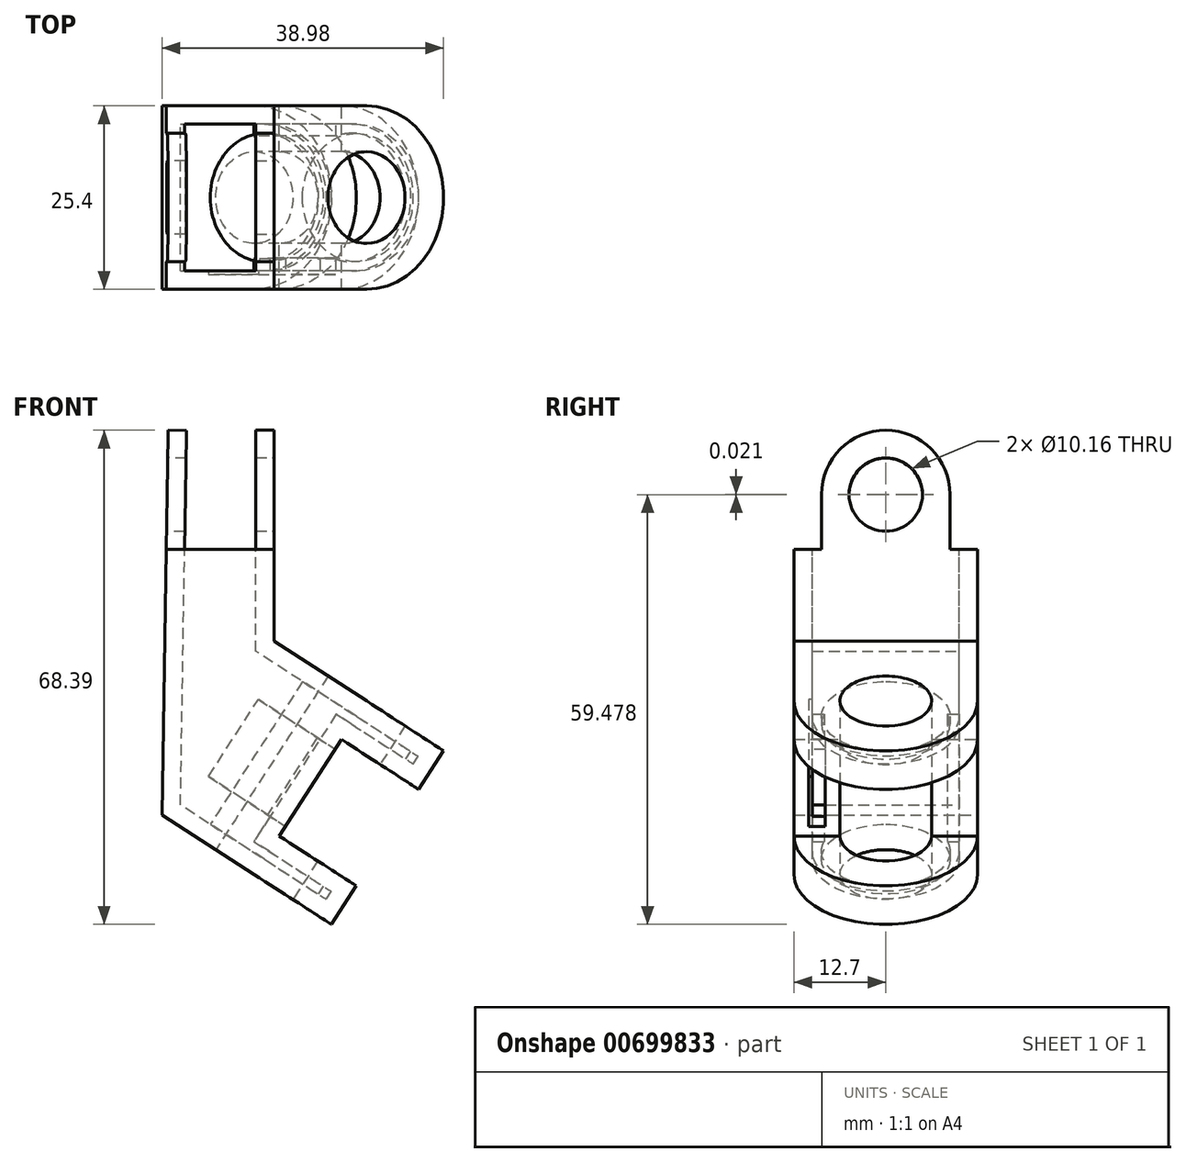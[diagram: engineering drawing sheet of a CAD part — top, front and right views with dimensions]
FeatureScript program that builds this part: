
annotation { "Feature Type Name" : "Feature", "Feature Type Description" : "" }
export const myFeature = defineFeature(function(context is Context, id is Id, definition is map)
    precondition{}
    {
        {
            var Q0;
            Q0=qCreatedBy(makeId("Front.planeOp"),FACE);
            var sketch = newSketch(context, id + "F0", { "sketchPlane" : qUnion([Q0])});
            skLineSegment(sketch, "E0", {"start": v(3.05, 0.95) * mm, "end": v(-9.73, 9.2) * mm});
            skLineSegment(sketch, "E1", {"start": v(-12.48, -23.08) * mm, "end": v(-25.26, -14.82) * mm});
            skLineSegment(sketch, "E2", {"start": v(-9.73, 9.2) * mm, "end": v(-9.73, 21.9) * mm});
            skLineSegment(sketch, "E3", {"start": v(-24.67, 21.9) * mm, "end": v(-9.73, 21.9) * mm});
            skLineSegment(sketch, "E4", {"start": v(-10.92, -20.66) * mm, "end": v(1.49, -1.46) * mm});
            skPoint(sketch, "E5.start.orphan", {"position": v(4.25, -16.85) * mm});
            skLineSegment(sketch, "E6", {"start": v(-10.92, -20.66) * mm, "end": v(-12.48, -23.08) * mm});
            skLineSegment(sketch, "E7", {"start": v(-12.48, -23.08) * mm, "end": v(3.05, 0.95) * mm});
            skPoint(sketch, "E8.orphan", {"position": v(-3.52, -28.87) * mm});
            skPoint(sketch, "E9.start.orphan", {"position": v(-1.96, -26.45) * mm});
            skPoint(sketch, "E10.start.orphan", {"position": v(10.45, -7.25) * mm});
            skPoint(sketch, "E11.orphan", {"position": v(12, -4.84) * mm});
            skLineSegment(sketch, "E12", {"start": v(-25.26, -14.82) * mm, "end": v(-24.67, 21.9) * mm});
            skSolve(sketch);
        }
        {
            var Q0;
            Q0=qSketchRegion(id+"F0",true);
            extrude(context, id + "F1", {"entities" : qUnion([Q0]), "depth" : 25.4 * mm});
        }
        {
            var Q0;
            Q0=makeQuery(id+"F1.opExtrude","SWEPT_FACE",FACE,{"disambiguationData":[OSD([sQuery(id+"F0.wireOp",EDGE,"E0")])]});
            var sketch = newSketch(context, id + "F2", { "sketchPlane" : qUnion([Q0])});
            skLineSegment(sketch, "E13", {"start": v(2.04, -25.4) * mm, "end": v(2.04, -17.78) * mm});
            skArc(sketch, "E14", {"start": v(2.04, -25.4) * mm, "mid": v(14.74, -12.7) * mm, "end": v(2.04, 0) * mm});
            skCircle(sketch, "E15", {"center": v(2.04, -12.7) * mm, "radius": 5.08 * mm});
            skLineSegment(sketch, "E16.trimOffspring", {"start": v(2.04, -7.62) * mm, "end": v(2.04, 0) * mm});
            skSolve(sketch);
        }
        {
            var Q0;
            {var subQ0=sQuery(id+"F2.wireOp",EDGE,"E13");Q0=makeQuery(id+"F2.imprint","IMPRINT",FACE,{"disambiguationData":[TD([[makeQuery(id+"F2.imprint","IMPRINT",EDGE,{"derivedFrom":subQ0}),-1.0]])]});}
            extrude(context, id + "F3", {"entities" : qUnion([Q0]), "operationType" : NewBodyOperationType.ADD, "depth" : -6.35 * mm});
        }
        {
            var Q0;
            Q0=makeQuery(id+"F1.opExtrude","SWEPT_FACE",FACE,{"disambiguationData":[OSD([sQuery(id+"F0.wireOp",EDGE,"E1")])]});
            var sketch = newSketch(context, id + "F4", { "sketchPlane" : qUnion([Q0])});
            skArc(sketch, "E17", {"start": v(2.04, 0) * mm, "mid": v(14.74, 12.7) * mm, "end": v(2.04, 25.4) * mm});
            skCircle(sketch, "E18", {"center": v(2.04, 12.7) * mm, "radius": 6.35 * mm});
            skSolve(sketch);
        }
        {
            var Q0;
            {var subQ0=sQuery(id+"F4.wireOp",EDGE,"E17");Q0=makeQuery(id+"F4.imprint","IMPRINT",FACE,{"disambiguationData":[TD([[makeQuery(id+"F4.imprint","IMPRINT",EDGE,{"derivedFrom":subQ0}),1.0]])]});}
            extrude(context, id + "F5", {"entities" : qUnion([Q0]), "operationType" : NewBodyOperationType.ADD, "depth" : -6.35 * mm});
        }
        {
            var Q0;
            Q0=sQuery(id+"F4.wireOp",VERTEX,"E17.center");
            var Q1;
            Q1=makeQuery(id+"F1.opExtrude","SWEPT_BODY",BODY,{"disambiguationData":[OSD([sQuery(id+"F0.wireOp",EDGE,"E0"),sQuery(id+"F0.wireOp",EDGE,"E1"),sQuery(id+"F0.wireOp",EDGE,"E2"),sQuery(id+"F0.wireOp",EDGE,"91f72571-9d86-468c-b467-24505ed81b32"),sQuery(id+"F0.wireOp",EDGE,"E3"),sQuery(id+"F0.wireOp",EDGE,"E7")])]});
            hole(context, id + "F6", {"style" : HoleStyle.SIMPLE, "endStyle" : HoleEndStyle.THROUGH, "holeDiameter" : 12.7 * mm, "isTappedThrough" : true, "tappedDepth" : 12.7 * mm, "tapClearance" : 3, "locations" : qUnion([Q0]), "scope" : qUnion([Q1])});
        }
        {
            var Q0;
            Q0=makeQuery(id+"F1.opExtrude","SWEPT_FACE",FACE,{"disambiguationData":[OSD([sQuery(id+"F0.wireOp",EDGE,"E3")])]});
            shell(context, id + "F7", {"entities" : qUnion([Q0]), "thickness" : 2.54 * mm});
        }
        {
            var Q0;
            Q0=makeQuery(id+"F1.opExtrude","SWEPT_FACE",FACE,{"disambiguationData":[OSD([sQuery(id+"F0.wireOp",EDGE,"E2")])]});
            var sketch = newSketch(context, id + "F8", { "sketchPlane" : qUnion([Q0])});
            skLineSegment(sketch, "E19", {"start": v(-12.7, 21.9) * mm, "end": v(-12.7, 29.53) * mm});
            skLineSegment(sketch, "E20", {"start": v(-21.6, 21.9) * mm, "end": v(-21.6, 29.53) * mm});
            skLineSegment(sketch, "E21", {"start": v(-3.81, 21.9) * mm, "end": v(-3.81, 29.53) * mm});
            skArc(sketch, "E22", {"start": v(-3.8, 29.53) * mm, "mid": v(-12.7, 38.42) * mm, "end": v(-21.6, 29.53) * mm});
            skCircle(sketch, "E23", {"center": v(-12.7, 29.53) * mm, "radius": 5.08 * mm});
            skSolve(sketch);
        }
        {
            var Q0;
            {var subQ1=sQuery(id+"F8.wireOp",EDGE,"E20");Q0=makeQuery(id+"F8.imprint","IMPRINT",FACE,{"disambiguationData":[TD([[makeQuery(id+"F8.imprint","IMPRINT",EDGE,{"derivedFrom":subQ1}),-1.0]])]});}
            extrude(context, id + "F9", {"entities" : qUnion([Q0]), "operationType" : NewBodyOperationType.ADD, "depth" : -2.54 * mm});
        }
        {
            var Q0;
            Q0=makeQuery(id+"F1.opExtrude","SWEPT_FACE",FACE,{"disambiguationData":[OSD([sQuery(id+"F0.wireOp",EDGE,"E12")])]});
            var sketch = newSketch(context, id + "F10", { "sketchPlane" : qUnion([Q0])});
            skLineSegment(sketch, "E24", {"start": v(3.81, 21.51) * mm, "end": v(3.81, 29.13) * mm});
            skLineSegment(sketch, "E25", {"start": v(21.6, 21.51) * mm, "end": v(21.6, 29.13) * mm});
            skArc(sketch, "E26", {"start": v(21.6, 29.13) * mm, "mid": v(12.7, 38.02) * mm, "end": v(3.81, 29.13) * mm});
            skCircle(sketch, "E27", {"center": v(12.7, 29.13) * mm, "radius": 5.08 * mm});
            skLineSegment(sketch, "E28", {"start": v(3.81, 29.13) * mm, "end": v(7.62, 29.13) * mm});
            skPoint(sketch, "E29.start.orphan", {"position": v(12.7, 21.51) * mm});
            skLineSegment(sketch, "E30.trimOffspring", {"start": v(12.7, 29.13) * mm, "end": v(21.6, 29.13) * mm});
            skSolve(sketch);
        }
        {
            var Q0;
            {var subQ5=sQuery(id+"F10.wireOp",EDGE,"E24");Q0=makeQuery(id+"F10.imprint","IMPRINT",FACE,{"disambiguationData":[TD([[makeQuery(id+"F10.imprint","IMPRINT",EDGE,{"derivedFrom":subQ5}),-1.0]])]});}
            var Q1;
            {var subQ0=sQuery(id+"F10.wireOp",EDGE,"E26");Q1=makeQuery(id+"F10.imprint","IMPRINT",FACE,{"disambiguationData":[TD([[makeQuery(id+"F10.imprint","IMPRINT",EDGE,{"derivedFrom":subQ0}),1.0]])]});}
            extrude(context, id + "F11", {"entities" : qUnion([Q0, Q1]), "operationType" : NewBodyOperationType.ADD, "depth" : -2.54 * mm});
        }
        {
            var Q0;
            {var subQ2=sQuery(id+"F0.wireOp",EDGE,"E7");var subQ3=sQuery(id+"F0.wireOp",EDGE,"E1");Q0=makeQuery(id+"F6.hole-0.boolean.opBoolean","SPLIT",FACE,{"disambiguationData":[TD([makeQuery(id+"F1.opExtrude","CAP_FACE",FACE,{"disambiguationData":[OSD([sQuery(id+"F0.wireOp",EDGE,"E0"),subQ3,sQuery(id+"F0.wireOp",EDGE,"E2"),sQuery(id+"F0.wireOp",EDGE,"E3"),subQ2,sQuery(id+"F0.wireOp",EDGE,"E12")])],"isStart":false})])],"derivedFrom":makeQuery(id+"F1.opExtrude","SWEPT_FACE",FACE,{"disambiguationData":[OSD([subQ2])]})});}
            var sketch = newSketch(context, id + "F12", { "sketchPlane" : qUnion([Q0])});
            skLineSegment(sketch, "E31", {"start": v(-25.4, -11.85) * mm, "end": v(-19.05, -11.85) * mm});
            skLineSegment(sketch, "E32.bottom", {"start": v(-21.08, -5.5) * mm, "end": v(-23.37, -5.5) * mm});
            skLineSegment(sketch, "E32.top", {"start": v(-21.08, -18.2) * mm, "end": v(-23.37, -18.2) * mm});
            skLineSegment(sketch, "E32.left", {"start": v(-21.08, -5.5) * mm, "end": v(-21.08, -18.2) * mm});
            skLineSegment(sketch, "E32.right", {"start": v(-23.37, -5.5) * mm, "end": v(-23.37, -18.2) * mm});
            skPoint(sketch, "E32.middle", {"position": v(-22.23, -11.85) * mm});
            skSolve(sketch);
        }
        {
            var Q0;
            {var subQ5=sQuery(id+"F12.wireOp",EDGE,"E32.top");Q0=makeQuery(id+"F12.imprint","IMPRINT",FACE,{"disambiguationData":[TD([[makeQuery(id+"F12.imprint","IMPRINT",EDGE,{"derivedFrom":subQ5}),-1.0]])]});}
            var Q1;
            {var subQ5=sQuery(id+"F12.wireOp",EDGE,"E32.bottom");Q1=makeQuery(id+"F12.imprint","IMPRINT",FACE,{"disambiguationData":[TD([[makeQuery(id+"F12.imprint","IMPRINT",EDGE,{"derivedFrom":subQ5}),1.0]])]});}
            extrude(context, id + "F13", {"entities" : qUnion([Q0, Q1]), "operationType" : NewBodyOperationType.REMOVE, "oppositeDirection" : true, "depth" : 12.7 * mm});
        }
    });
